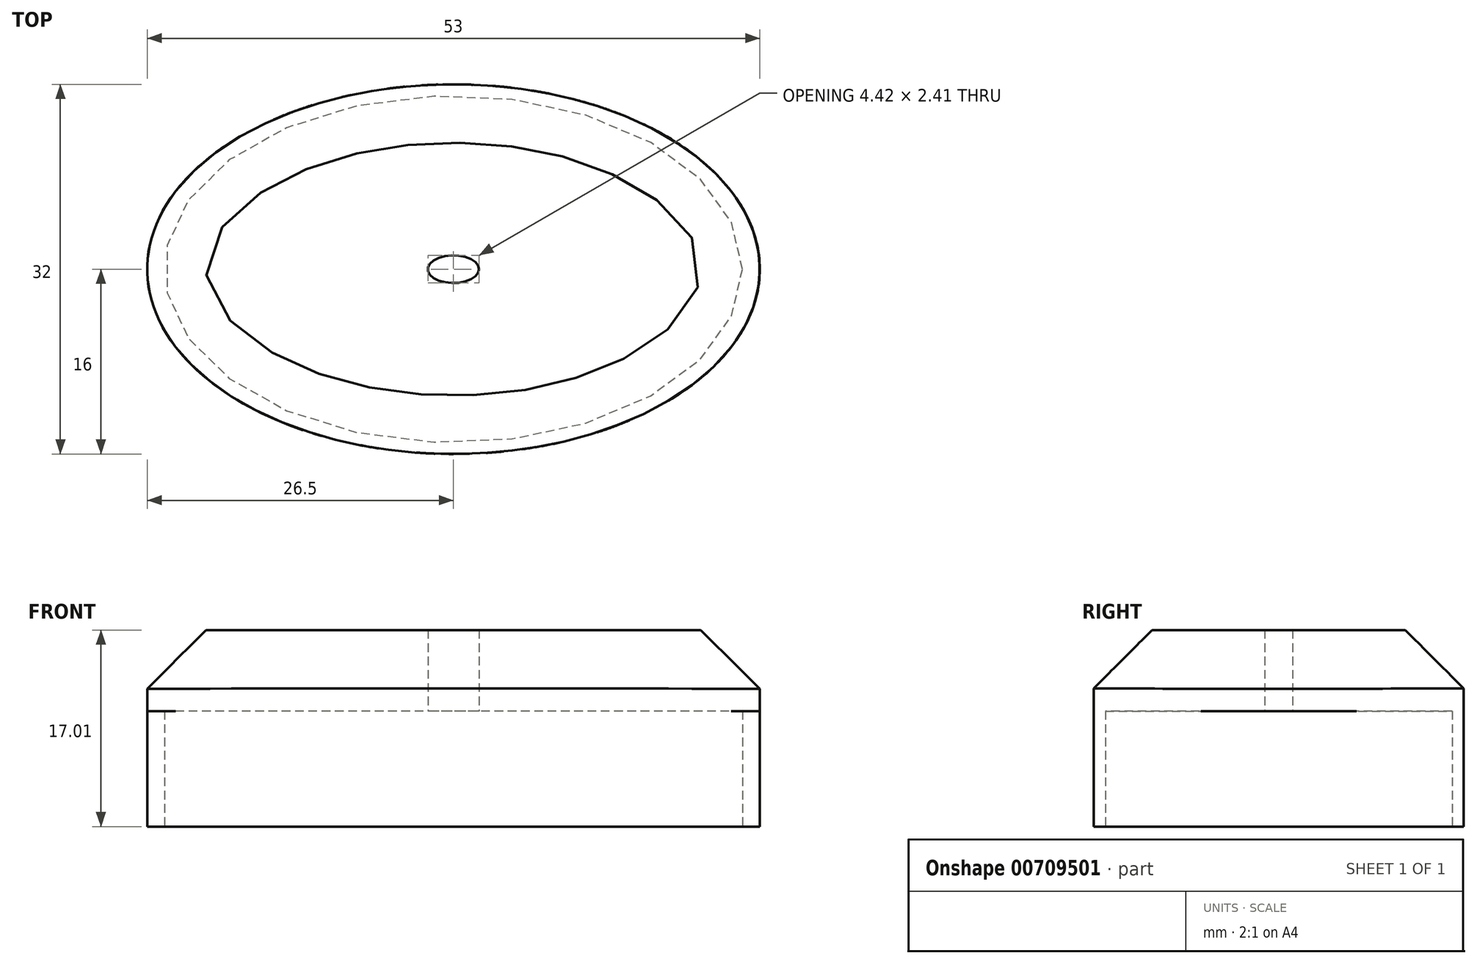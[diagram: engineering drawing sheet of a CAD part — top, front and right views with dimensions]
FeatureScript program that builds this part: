
annotation { "Feature Type Name" : "Feature", "Feature Type Description" : "" }
export const myFeature = defineFeature(function(context is Context, id is Id, definition is map)
    precondition{}
    {
        {
            var Q0;
            Q0=qCreatedBy(makeId("Top.planeOp"),FACE);
            var sketch = newSketch(context, id + "F0", { "sketchPlane" : qUnion([Q0])});
            skEllipse(sketch, "E0", {"center": v(0, 0) * mm, "majorRadius": 25 * mm, "minorRadius": 15 * mm, "majorAxis": v(1, 0)});
            skEllipse(sketch, "E1", {"center": v(0, 0) * mm, "majorRadius": 26.5 * mm, "minorRadius": 16 * mm, "majorAxis": v(1, 0)});
            skSolve(sketch);
        }
        {
            var Q0;
            Q0=makeQuery(id+"F0.imprint","IMPRINT",FACE,{"disambiguationData":[TD([[makeQuery(id+"F0.imprint","IMPRINT",EDGE,{"derivedFrom":sQuery(id+"F0.wireOp",EDGE,"E0")}),-1.0]])]});
            extrude(context, id + "F1", {"entities" : qUnion([Q0]), "depth" : 10 * mm, "offsetDistance" : 25.4 * mm});
        }
        {
            var Q0;
            Q0=makeQuery(id+"F1.opExtrude","CAP_FACE",FACE,{"disambiguationData":[OSD([sQuery(id+"F0.wireOp",EDGE,"E0"),sQuery(id+"F0.wireOp",EDGE,"E1")])],"isStart":false});
            var sketch = newSketch(context, id + "F2", { "sketchPlane" : qUnion([Q0])});
            skEllipse(sketch, "E2", {"center": v(0, 0) * mm, "majorRadius": 26.49 * mm, "minorRadius": 16.03 * mm, "majorAxis": v(1, 0)});
            skEllipse(sketch, "E3", {"center": v(0, 0) * mm, "majorRadius": 2.2 * mm, "minorRadius": 1.2 * mm, "majorAxis": v(1, 0)});
            skSolve(sketch);
        }
        {
            var Q0;
            Q0=makeQuery(id+"F2.imprint","IMPRINT",FACE,{"disambiguationData":[TD([[makeQuery(id+"F2.imprint","IMPRINT",EDGE,{"derivedFrom":sQuery(id+"F2.wireOp",EDGE,"E3")}),-1.0]])]});
            cPlane(context, id + "F3", {"entities" : qUnion([Q0]), "cplaneType" : CPlaneType.OFFSET, "offset" : 12.7 * mm, "width" : 152.4 * mm, "height" : 152.4 * mm});
        }
        {
            var Q0;
            Q0=makeQuery(id+"F2.imprint","IMPRINT",FACE,{"disambiguationData":[TD([[makeQuery(id+"F2.imprint","IMPRINT",EDGE,{"derivedFrom":makeQuery(id+"F1.opExtrude","CAP_EDGE",EDGE,{"disambiguationData":[OSD([sQuery(id+"F0.wireOp",EDGE,"E0")])],"isStart":false})}),-1.0]])]});
            var Q1;
            Q1=makeQuery(id+"F2.imprint","IMPRINT",FACE,{"disambiguationData":[TD([[makeQuery(id+"F2.imprint","IMPRINT",EDGE,{"derivedFrom":sQuery(id+"F2.wireOp",EDGE,"E3")}),-1.0]])]});
            extrude(context, id + "F4", {"entities" : qUnion([Q0, Q1]), "operationType" : NewBodyOperationType.ADD, "depth" : 7 * mm, "offsetDistance" : 25.4 * mm});
        }
        {
            var Q0;
            {var subQ0=sQuery(id+"F2.wireOp",EDGE,"E2");var subQ1=makeQuery(id+"F1.opExtrude","CAP_EDGE",EDGE,{"disambiguationData":[OSD([sQuery(id+"F0.wireOp",EDGE,"E1")])],"isStart":false});Q0=makeQuery(id+"F4.opExtrude","CAP_EDGE",EDGE,{"disambiguationData":[OSD([subQ0]),TDD([makeQuery(id+"F2.imprint","IMPRINT",EDGE,{"disambiguationData":[TD([[makeQuery(id+"F2.imprint","INTERSECT",VERTEX,{"disambiguationData":[OD(0.0)],"derivedFrom":[subQ1,subQ0]}),-1.0]])],"derivedFrom":subQ0})])],"isStart":false});}
            chamfer(context, id + "F5", {"entities" : qUnion([Q0]), "width" : 5.08 * mm, "tangentPropagation" : true});
        }
    });
